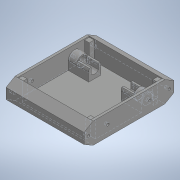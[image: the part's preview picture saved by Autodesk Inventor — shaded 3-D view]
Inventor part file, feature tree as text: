
AUTODESK INVENTOR PART (.ipt)
format: ipt  version: 2020 (Build 240168000, 168)  size: 265,728 bytes
history: native  units: in
note: dims shown in document units (in); Inventor stores cm internally (conversion verified against a paired STEP export)
features: extrude x8, sketch x8, projected_geometry x4, mirror x3
ambient origin geometry x8: Origin, YZ Plane, XZ Plane, XY Plane, X Axis, Y Axis, Z Axis, Center Point
bodies: Solid1 (feature_tree)
feature tree (23):
  extrude  "Extrusion1"  Depth=5.9055in
  extrude  "Extrusion2"  TaperAngle=0.0deg  [1 undecoded]
  extrude  "Extrusion3"  Depth=1.2598in
  extrude  "Extrusion4"  Depth=0.315in
  extrude  "Extrusion5"  TaperAngle=0.0deg  [1 undecoded]
  extrude  "Extrusion6"  Depth=0.689in
  mirror  "Mirror1"
  extrude  "Extrusion7"  Depth=0.0787in
  mirror  "Mirror2"
  extrude  "Extrusion8"  Depth=0.2756in
  mirror  "Mirror3"
  sketch  "Sketch1"  dims[d0=1.378in d1=5.9055in]
  sketch  "Sketch2"  dims[d2=5.1181in d3=0.0in]
  projected_geometry  "Projected Loop1"
  sketch  "Sketch3"  dims[d4=0.1575in d5=1.2598in]
  projected_geometry  "Projected Loop2"
  projected_geometry  "Projected Loop3"
  sketch  "Sketch4"  dims[d6=0.0in d8=0.315in]
  sketch  "Sketch5"  dims[d10=1.1898in d11=0.0in]
  projected_geometry  "Projected Loop4"
  sketch  "Sketch6"  dims[d12=0.6496in d13=0.689in]
  sketch  "Sketch7"  dims[d14=1.5748in d15=0.0787in]
  sketch  "Sketch9"  dims[d16=0.5512in d17=0.0in d18=0.6102in d19=0.4803in d20=0.7874in d21=0.0in d22=0.1654in d23=6.063in d24=0.0in d25=0.5967in d26=0.1575in d27=1.5748in d28=0.0in d29=0.0in d30=0.1575in d31=0.2756in d32=0.0in]
note: 2 required parameter values undecoded (feature->parameter linkage not recoverable at this tier; creation-order binding heuristic only, values carry confidence <= 0.55)
